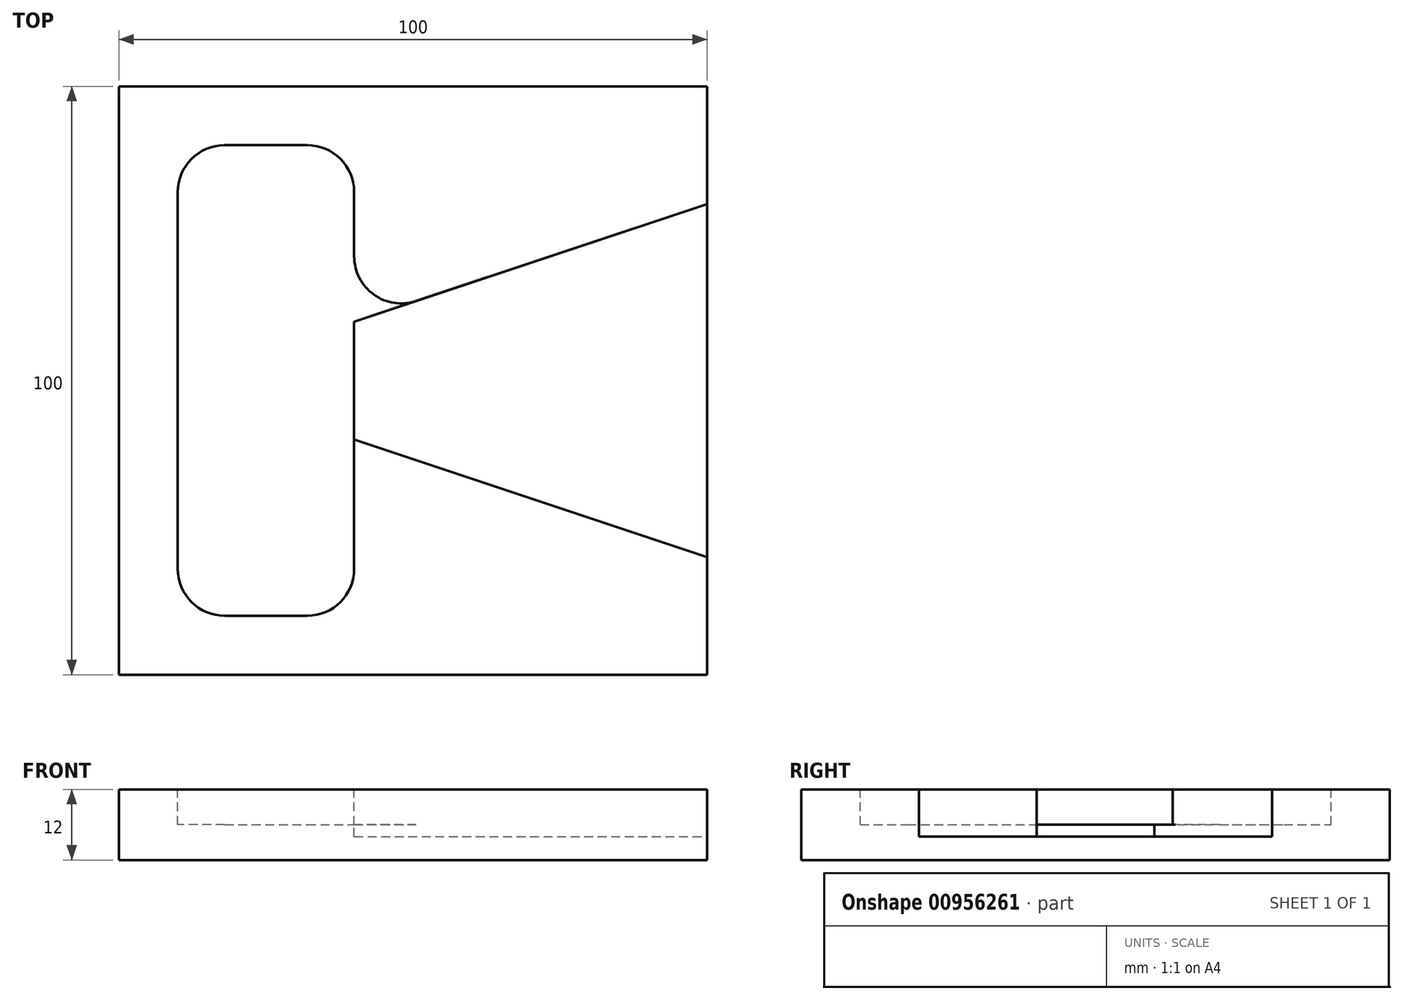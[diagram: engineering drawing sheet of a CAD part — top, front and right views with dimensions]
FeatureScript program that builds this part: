
annotation { "Feature Type Name" : "Feature", "Feature Type Description" : "" }
export const myFeature = defineFeature(function(context is Context, id is Id, definition is map)
    precondition{}
    {
        {
            var Q0;
            Q0=qCreatedBy(makeId("Top.planeOp"),FACE);
            var sketch = newSketch(context, id + "F0", { "sketchPlane" : qUnion([Q0])});
            skLineSegment(sketch, "E0.bottom", {"start": v(0, 0) * mm, "end": v(100, 0) * mm});
            skLineSegment(sketch, "E0.top", {"start": v(0, 100) * mm, "end": v(100, 100) * mm});
            skLineSegment(sketch, "E0.left", {"start": v(0, 0) * mm, "end": v(0, 100) * mm});
            skLineSegment(sketch, "E0.right", {"start": v(100, 0) * mm, "end": v(100, 100) * mm});
            skSolve(sketch);
        }
        {
            var Q0;
            Q0=makeQuery(id+"F0.imprint","IMPRINT",FACE,{"disambiguationData":[TD([[makeQuery(id+"F0.imprint","IMPRINT",EDGE,{"derivedFrom":sQuery(id+"F0.wireOp",EDGE,"E0.bottom")}),1.0]])]});
            extrude(context, id + "F1", {"entities" : qUnion([Q0]), "depth" : 12 * mm, "offsetDistance" : 25 * mm});
        }
        {
            var Q0;
            Q0=makeQuery(id+"F1.opExtrude","CAP_FACE",FACE,{"disambiguationData":[OSD([sQuery(id+"F0.wireOp",EDGE,"E0.bottom"),sQuery(id+"F0.wireOp",EDGE,"E0.top"),sQuery(id+"F0.wireOp",EDGE,"E0.left"),sQuery(id+"F0.wireOp",EDGE,"E0.right")])],"isStart":false});
            var sketch = newSketch(context, id + "F2", { "sketchPlane" : qUnion([Q0])});
            skLineSegment(sketch, "E1.bottom", {"start": v(10, 10) * mm, "end": v(40, 10) * mm});
            skLineSegment(sketch, "E1.top", {"start": v(10, 90) * mm, "end": v(40, 90) * mm});
            skLineSegment(sketch, "E1.left", {"start": v(10, 10) * mm, "end": v(10, 90) * mm});
            skLineSegment(sketch, "E1.right", {"start": v(40, 10) * mm, "end": v(40, 90) * mm});
            skSolve(sketch);
        }
        {
            var Q0;
            Q0=makeQuery(id+"F2.imprint","IMPRINT",FACE,{"disambiguationData":[TD([[makeQuery(id+"F2.imprint","IMPRINT",EDGE,{"derivedFrom":sQuery(id+"F2.wireOp",EDGE,"E1.bottom")}),1.0]])]});
            extrude(context, id + "F3", {"entities" : qUnion([Q0]), "operationType" : NewBodyOperationType.REMOVE, "oppositeDirection" : true, "depth" : 6 * mm, "offsetDistance" : 25 * mm});
        }
        {
            var Q0;
            Q0=makeQuery(id+"F1.opExtrude","CAP_FACE",FACE,{"disambiguationData":[OSD([sQuery(id+"F0.wireOp",EDGE,"E0.bottom"),sQuery(id+"F0.wireOp",EDGE,"E0.top"),sQuery(id+"F0.wireOp",EDGE,"E0.left"),sQuery(id+"F0.wireOp",EDGE,"E0.right")])],"isStart":false});
            var sketch = newSketch(context, id + "F4", { "sketchPlane" : qUnion([Q0])});
            skLineSegment(sketch, "E2", {"start": v(10, 50) * mm, "end": v(100, 80) * mm});
            skLineSegment(sketch, "E3", {"start": v(100, 80) * mm, "end": v(100, 20) * mm});
            skLineSegment(sketch, "E4", {"start": v(100, 20) * mm, "end": v(10, 50) * mm});
            skSolve(sketch);
        }
        {
            var Q0;
            {var subQ0=sQuery(id+"F4.wireOp",EDGE,"E3");Q0=makeQuery(id+"F4.imprint","IMPRINT",FACE,{"disambiguationData":[TD([[makeQuery(id+"F4.imprint","IMPRINT",EDGE,{"derivedFrom":subQ0}),1.0]])]});}
            var Q1;
            {var subQ1=sQuery(id+"F4.wireOp",EDGE,"E2");var subQ3=makeQuery(id+"F3.boolean.opBoolean","COPY",EDGE,{"derivedFrom":makeQuery(id+"F3.opExtrude","CAP_EDGE",EDGE,{"disambiguationData":[OSD([sQuery(id+"F2.wireOp",EDGE,"E1.right")])],"isStart":true})});var subQ4=makeQuery(id+"F4.imprint","INTERSECT",VERTEX,{"derivedFrom":[subQ3,subQ1]});Q1=makeQuery(id+"F4.imprint","IMPRINT",FACE,{"disambiguationData":[TD([[makeQuery(id+"F4.imprint","IMPRINT",EDGE,{"disambiguationData":[TD([[subQ4,1.0]])],"derivedFrom":subQ3}),1.0]])]});}
            extrude(context, id + "F5", {"entities" : qUnion([Q0, Q1]), "operationType" : NewBodyOperationType.REMOVE, "oppositeDirection" : true, "depth" : 8 * mm, "offsetDistance" : 25 * mm});
        }
        {
            var Q0;
            Q0=makeQuery(id+"F5.boolean.opBoolean","COPY",EDGE,{"derivedFrom":makeQuery(id+"F5.opExtrude","SWEPT_EDGE",EDGE,{"disambiguationData":[OSD([sQuery(id+"F2.wireOp",EDGE,"E1.left"),sQuery(id+"F4.wireOp",EDGE,"E2"),sQuery(id+"F4.wireOp",EDGE,"E4")])]})});
            var Q1;
            Q1=makeQuery(id+"F3.boolean.opBoolean","COPY",EDGE,{"derivedFrom":makeQuery(id+"F3.opExtrude","SWEPT_EDGE",EDGE,{"disambiguationData":[OSD([sQuery(id+"F2.wireOp",EDGE,"E1.top"),sQuery(id+"F2.wireOp",EDGE,"E1.left")])]})});
            var Q2;
            Q2=makeQuery(id+"F3.boolean.opBoolean","COPY",EDGE,{"derivedFrom":makeQuery(id+"F3.opExtrude","SWEPT_EDGE",EDGE,{"disambiguationData":[OSD([sQuery(id+"F2.wireOp",EDGE,"E1.bottom"),sQuery(id+"F2.wireOp",EDGE,"E1.left")])]})});
            var Q3;
            Q3=makeQuery(id+"F3.boolean.opBoolean","COPY",EDGE,{"derivedFrom":makeQuery(id+"F3.opExtrude","SWEPT_EDGE",EDGE,{"disambiguationData":[OSD([sQuery(id+"F2.wireOp",EDGE,"E1.top"),sQuery(id+"F2.wireOp",EDGE,"E1.right")])]})});
            var Q4;
            Q4=makeQuery(id+"F3.boolean.opBoolean","COPY",EDGE,{"derivedFrom":makeQuery(id+"F3.opExtrude","SWEPT_EDGE",EDGE,{"disambiguationData":[OSD([sQuery(id+"F2.wireOp",EDGE,"E1.bottom"),sQuery(id+"F2.wireOp",EDGE,"E1.right")])]})});
            var Q5;
            Q5=makeQuery(id+"F5.boolean.opBoolean","COPY",EDGE,{"derivedFrom":makeQuery(id+"F5.opExtrude","SWEPT_EDGE",EDGE,{"disambiguationData":[OSD([sQuery(id+"F0.wireOp",EDGE,"E0.right"),sQuery(id+"F4.wireOp",EDGE,"E3"),sQuery(id+"F4.wireOp",EDGE,"E4")])]})});
            var Q6;
            Q6=makeQuery(id+"F5.boolean.opBoolean","COPY",EDGE,{"derivedFrom":makeQuery(id+"F5.opExtrude","SWEPT_EDGE",EDGE,{"disambiguationData":[OSD([sQuery(id+"F0.wireOp",EDGE,"E0.right"),sQuery(id+"F4.wireOp",EDGE,"E2"),sQuery(id+"F4.wireOp",EDGE,"E3")])]})});
            var Q7;
            Q7=makeQuery(id+"F5.boolean.opBoolean","INTERSECT",EDGE,{"derivedFrom":[makeQuery(id+"F3.boolean.opBoolean","COPY",FACE,{"derivedFrom":makeQuery(id+"F3.opExtrude","SWEPT_FACE",FACE,{"disambiguationData":[OSD([sQuery(id+"F2.wireOp",EDGE,"E1.right")])]})}),makeQuery(id+"F5.opExtrude","SWEPT_FACE",FACE,{"disambiguationData":[OSD([sQuery(id+"F4.wireOp",EDGE,"E2")])]})]});
            var Q8;
            Q8=makeQuery(id+"F5.boolean.opBoolean","INTERSECT",EDGE,{"derivedFrom":[makeQuery(id+"F3.boolean.opBoolean","COPY",FACE,{"derivedFrom":makeQuery(id+"F3.opExtrude","SWEPT_FACE",FACE,{"disambiguationData":[OSD([sQuery(id+"F2.wireOp",EDGE,"E1.right")])]})}),makeQuery(id+"F5.opExtrude","SWEPT_FACE",FACE,{"disambiguationData":[OSD([sQuery(id+"F4.wireOp",EDGE,"E4")])]})]});
            fillet(context, id + "F6", {"entities" : qUnion([Q0, Q1, Q2, Q3, Q4, Q5, Q6, Q7, Q8]), "radius" : 8 * mm, "tangentPropagation" : true, "allowEdgeOverflow" : false});
        }
    });
